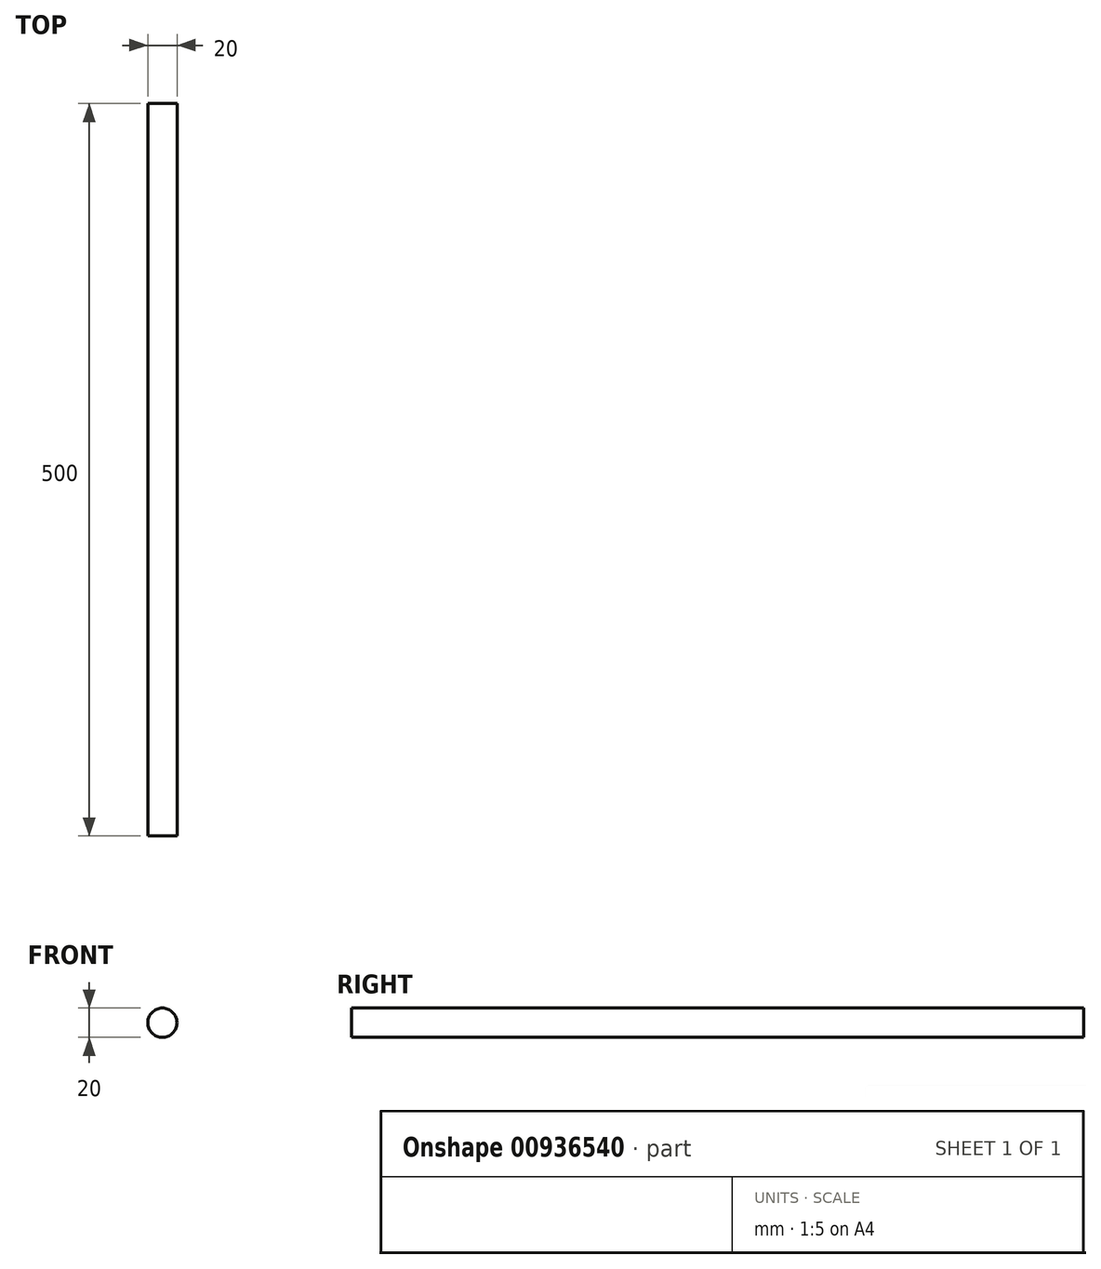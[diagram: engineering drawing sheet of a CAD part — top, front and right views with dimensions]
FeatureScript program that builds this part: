
annotation { "Feature Type Name" : "Feature", "Feature Type Description" : "" }
export const myFeature = defineFeature(function(context is Context, id is Id, definition is map)
    precondition{}
    {
        {
            var Q0;
            Q0=qCreatedBy(makeId("Front.planeOp"),FACE);
            var sketch = newSketch(context, id + "F0", { "sketchPlane" : qUnion([Q0])});
            skCircle(sketch, "E0", {"center": v(0, 0) * mm, "radius": 10 * mm});
            skSolve(sketch);
        }
        {
            var Q0;
            Q0=makeQuery(id+"F0.imprint","IMPRINT",FACE,{"disambiguationData":[TD([[makeQuery(id+"F0.imprint","IMPRINT",EDGE,{"derivedFrom":sQuery(id+"F0.wireOp",EDGE,"E0")}),1.0]])]});
            extrude(context, id + "F1", {"entities" : qUnion([Q0]), "depth" : 500 * mm, "offsetDistance" : 25.4 * mm});
        }
    });
